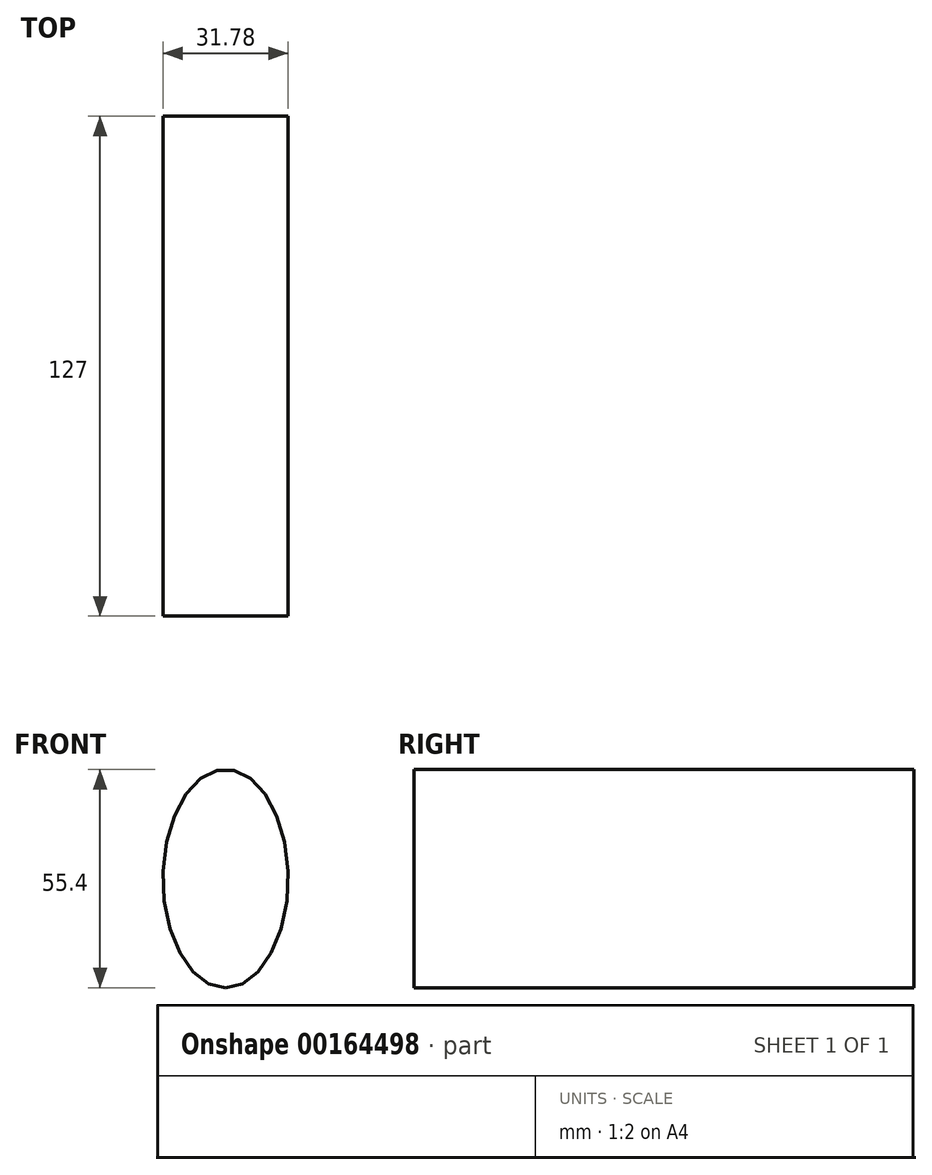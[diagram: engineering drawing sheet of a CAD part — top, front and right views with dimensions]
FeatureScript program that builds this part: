
annotation { "Feature Type Name" : "Feature", "Feature Type Description" : "" }
export const myFeature = defineFeature(function(context is Context, id is Id, definition is map)
    precondition{}
    {
        {
            var Q0;
            Q0=qCreatedBy(makeId("Front.planeOp"),FACE);
            var sketch = newSketch(context, id + "F0", { "sketchPlane" : qUnion([Q0])});
            skEllipse(sketch, "E0", {"center": v(15.89, 0) * mm, "majorRadius": 15.89 * mm, "minorRadius": 27.7 * mm, "majorAxis": v(-1, 0)});
            skSolve(sketch);
        }
        {
            var Q0;
            Q0=makeQuery(id+"F0.imprint","IMPRINT",FACE,{"disambiguationData":[TD([[makeQuery(id+"F0.imprint","IMPRINT",EDGE,{"derivedFrom":sQuery(id+"F0.wireOp",EDGE,"E0")}),1.0]])]});
            extrude(context, id + "F1", {"entities" : qUnion([Q0]), "depth" : 127 * mm});
        }
    });
